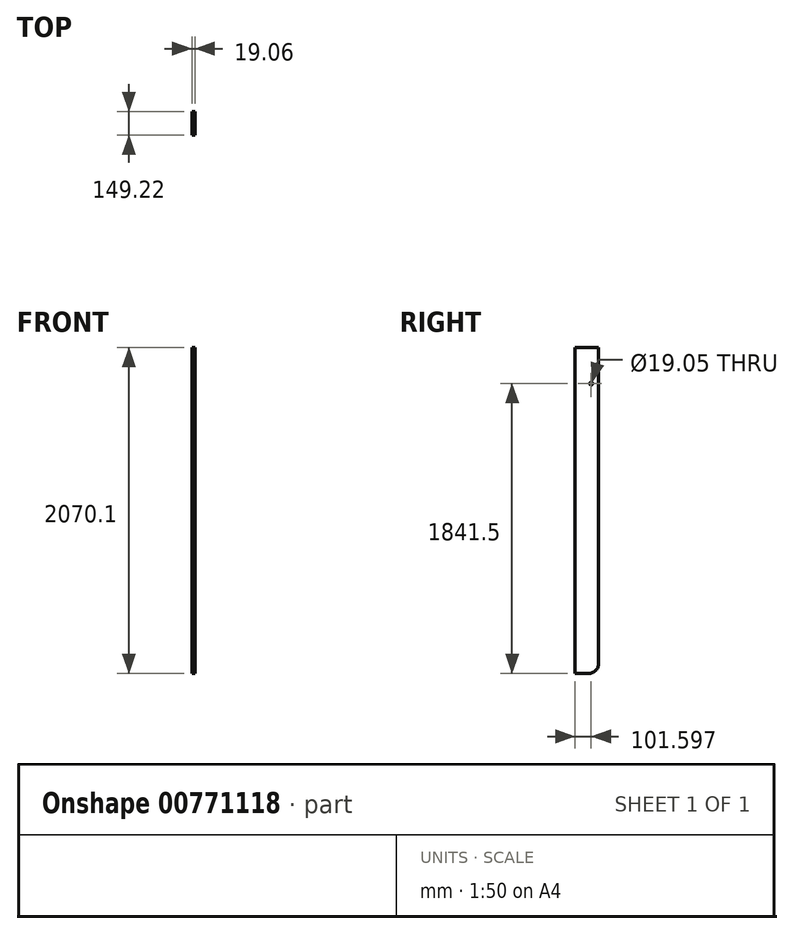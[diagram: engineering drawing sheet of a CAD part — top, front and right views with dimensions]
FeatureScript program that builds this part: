
annotation { "Feature Type Name" : "Feature", "Feature Type Description" : "" }
export const myFeature = defineFeature(function(context is Context, id is Id, definition is map)
    precondition{}
    {
        {
            var Q0;
            Q0=qCreatedBy(makeId("Top.planeOp"),FACE);
            var sketch = newSketch(context, id + "F0", { "sketchPlane" : qUnion([Q0])});
            skLineSegment(sketch, "E0.bottom", {"start": v(-9.52, 74.61) * mm, "end": v(9.53, 74.61) * mm});
            skLineSegment(sketch, "E0.top", {"start": v(-9.53, -74.61) * mm, "end": v(9.52, -74.61) * mm});
            skLineSegment(sketch, "E0.left", {"start": v(-9.52, 74.61) * mm, "end": v(-9.53, -74.61) * mm});
            skLineSegment(sketch, "E0.right", {"start": v(9.53, 74.61) * mm, "end": v(9.52, -74.61) * mm});
            skPoint(sketch, "E0.middle", {"position": v(0, 0) * mm});
            skSolve(sketch);
        }
        {
            var Q0;
            Q0 = qSketchRegion(id + "F0", true);
            extrude(context, id + "F1", {"entities" : qUnion([Q0]), "endBound" : BoundingType.SYMMETRIC, "depth" : 2070.1 * mm, "offsetDistance" : 25.4 * mm});
        }
        {
            var Q0;
            Q0=makeQuery(id+"F1.opExtrude","CAP_EDGE",EDGE,{"disambiguationData":[OSD([sQuery(id+"F0.wireOp",EDGE,"E0.bottom")])],"isStart":true});
            fillet(context, id + "F2", {"entities" : qUnion([Q0]), "radius" : 63.5 * mm, "tangentPropagation" : true, "allowEdgeOverflow" : false});
        }
        {
            var Q0;
            Q0=makeQuery(id+"F1.opExtrude","SWEPT_FACE",FACE,{"disambiguationData":[OSD([sQuery(id+"F0.wireOp",EDGE,"E0.right")])]});
            var sketch = newSketch(context, id + "F3", { "sketchPlane" : qUnion([Q0])});
            skCircle(sketch, "E1", {"center": v(26.99, 806.45) * mm, "radius": 12.7 * mm, "construction": true});
            skSolve(sketch);
        }
        {
            var Q0;
            Q0=sQuery(id+"F3.wireOp",VERTEX,"E1.center");
            var Q1;
            Q1=makeQuery(id+"F1.opExtrude","SWEPT_BODY",BODY,{"disambiguationData":[OSD([sQuery(id+"F0.wireOp",EDGE,"E0.bottom"),sQuery(id+"F0.wireOp",EDGE,"E0.top"),sQuery(id+"F0.wireOp",EDGE,"E0.left"),sQuery(id+"F0.wireOp",EDGE,"E0.right")])]});
            hole(context, id + "F4", {"style" : HoleStyle.SIMPLE, "endStyle" : HoleEndStyle.THROUGH, "holeDiameter" : 19.05 * mm, "majorDiameter" : 6.35 * mm, "isTappedThrough" : true, "tappedDepth" : 12.7 * mm, "tapClearance" : 3, "locations" : qUnion([Q0]), "scope" : qUnion([Q1])});
        }
    });
